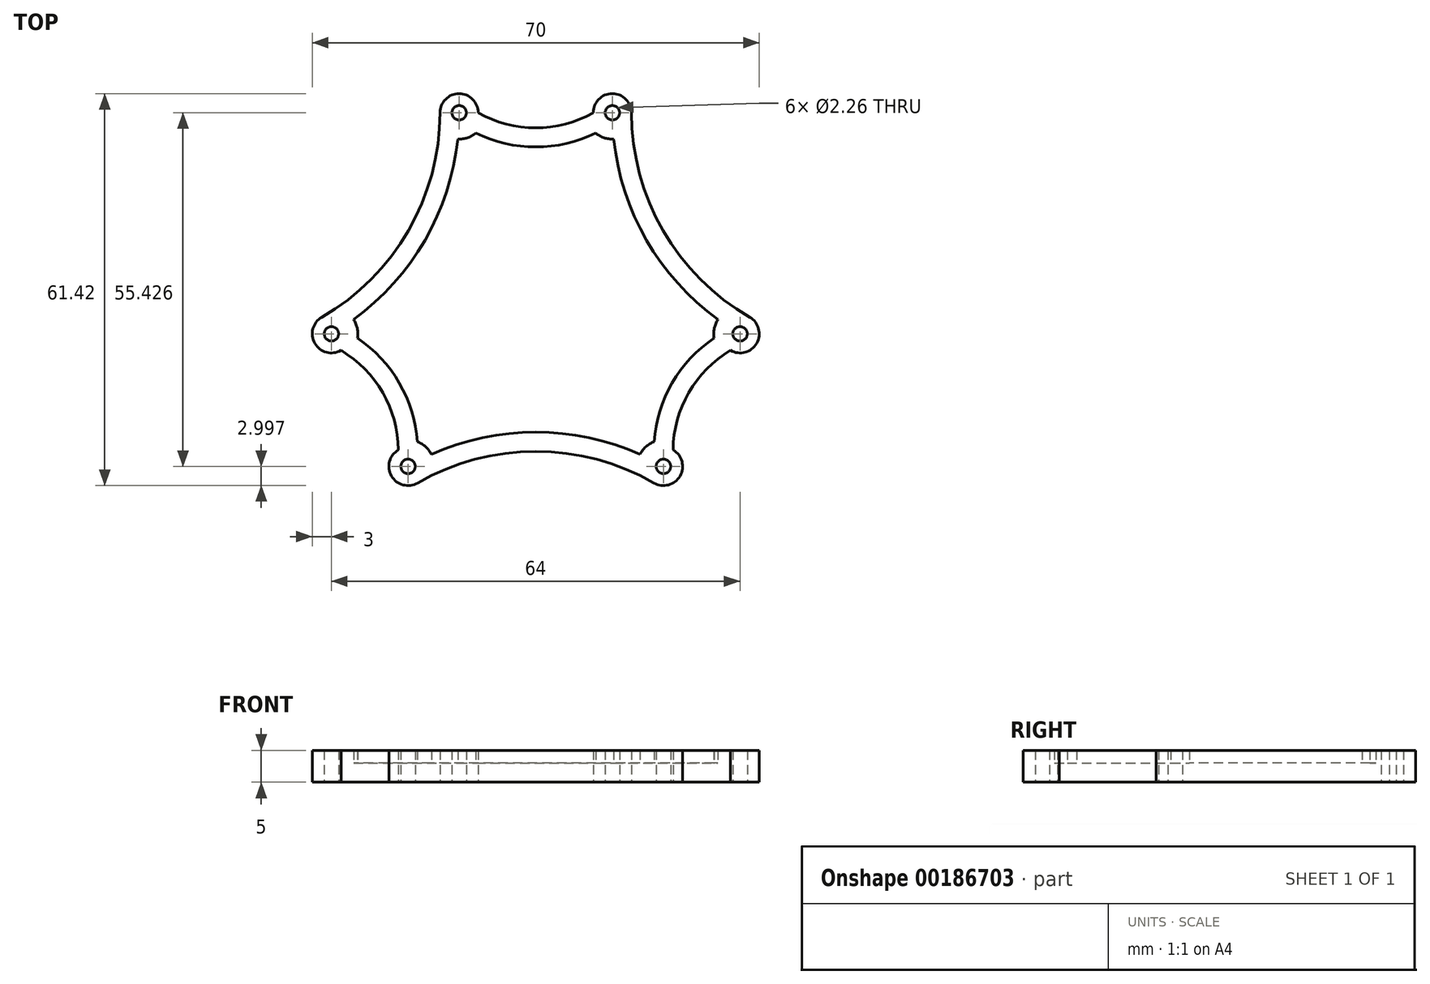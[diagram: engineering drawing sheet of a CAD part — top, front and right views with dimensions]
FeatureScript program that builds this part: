
annotation { "Feature Type Name" : "Feature", "Feature Type Description" : "" }
export const myFeature = defineFeature(function(context is Context, id is Id, definition is map)
    precondition{}
    {
        {
            var Q0;
            Q0=qCreatedBy(makeId("Top.planeOp"),FACE);
            var sketch = newSketch(context, id + "F0", { "sketchPlane" : qUnion([Q0])});
            skPoint(sketch, "E0.center", {"position": v(0, 0) * mm});
            skLineSegment(sketch, "E1", {"start": v(0, 0) * mm, "end": v(0, 30.02) * mm, "construction": true});
            skLineSegment(sketch, "E2", {"start": v(0, 30.02) * mm, "end": v(-12, 30.02) * mm, "construction": true});
            skLineSegment(sketch, "E3", {"start": v(0, 30.02) * mm, "end": v(12, 30.02) * mm, "construction": true});
            skLineSegment(sketch, "E4", {"start": v(0, 0) * mm, "end": v(26, -15.01) * mm, "construction": true});
            skLineSegment(sketch, "E5", {"start": v(32, -4.62) * mm, "end": v(26, -15.01) * mm, "construction": true});
            skLineSegment(sketch, "E6", {"start": v(20, -25.4) * mm, "end": v(26, -15.01) * mm, "construction": true});
            skLineSegment(sketch, "E7", {"start": v(0, 0) * mm, "end": v(-26, -15.01) * mm, "construction": true});
            skLineSegment(sketch, "E8", {"start": v(-20, -25.4) * mm, "end": v(-26, -15.01) * mm, "construction": true});
            skLineSegment(sketch, "E9", {"start": v(-32, -4.62) * mm, "end": v(-26, -15.01) * mm, "construction": true});
            skCircle(sketch, "E10", {"center": v(0, 0) * mm, "radius": 20 * mm, "construction": true});
            skSolve(sketch);
        }
        {
            var Q0;
            Q0=qCreatedBy(makeId("Top.planeOp"),FACE);
            var sketch = newSketch(context, id + "F1", { "sketchPlane" : qUnion([Q0])});
            skArc(sketch, "E11", {"start": v(-9, 30.02) * mm, "mid": v(-12, 33.02) * mm, "end": v(-15, 30.02) * mm});
            skArc(sketch, "E12.MirrorCS", {"start": v(9, 30.02) * mm, "mid": v(12, 33.02) * mm, "end": v(15, 30.02) * mm});
            skArc(sketch, "E13", {"start": v(-9, 30.02) * mm, "mid": v(0, 27.67) * mm, "end": v(9, 30.02) * mm});
            skArc(sketch, "E14.1.2", {"start": v(21.5, -22.8) * mm, "mid": v(22.6, -26.9) * mm, "end": v(18.5, -28) * mm});
            skArc(sketch, "E14.1.3", {"start": v(30.5, -7.22) * mm, "mid": v(23.96, -13.83) * mm, "end": v(21.5, -22.8) * mm});
            skArc(sketch, "E14.1.4", {"start": v(30.5, -7.22) * mm, "mid": v(34.6, -6.12) * mm, "end": v(33.5, -2.02) * mm});
            skArc(sketch, "E14.2.2", {"start": v(-30.5, -7.22) * mm, "mid": v(-34.6, -6.12) * mm, "end": v(-33.5, -2.02) * mm});
            skArc(sketch, "E14.2.3", {"start": v(-21.5, -22.8) * mm, "mid": v(-23.96, -13.83) * mm, "end": v(-30.5, -7.22) * mm});
            skArc(sketch, "E14.2.4", {"start": v(-21.5, -22.8) * mm, "mid": v(-22.6, -26.9) * mm, "end": v(-18.5, -28) * mm});
            skPoint(sketch, "E14.center", {"position": v(0, 0) * mm});
            skLineSegment(sketch, "E14.anchor1", {"start": v(0, 0) * mm, "end": v(-15, 13.23) * mm, "construction": true});
            skLineSegment(sketch, "E14.anchor2", {"start": v(0, 0) * mm, "end": v(-3.96, -19.6) * mm, "construction": true});
            skArc(sketch, "E15", {"start": v(15, 30.02) * mm, "mid": v(19.96, 11.52) * mm, "end": v(33.5, -2.02) * mm});
            skArc(sketch, "E16.1.0", {"start": v(-33.5, -2.02) * mm, "mid": v(-19.96, 11.52) * mm, "end": v(-15, 30.02) * mm});
            skArc(sketch, "E16.2.0", {"start": v(18.5, -28) * mm, "mid": v(0, -23.04) * mm, "end": v(-18.5, -28) * mm});
            skSolve(sketch);
        }
        {
            var Q0;
            Q0=makeQuery(id+"F1.imprint","IMPRINT",FACE,{"disambiguationData":[TD([[makeQuery(id+"F1.imprint","IMPRINT",EDGE,{"derivedFrom":sQuery(id+"F1.wireOp",EDGE,"E11")}),1.0]])]});
            extrude(context, id + "F2", {"entities" : qUnion([Q0]), "depth" : 5 * mm});
        }
        {
            var Q0;
            Q0=sQuery(id+"F0.wireOp",VERTEX,"E2.end");
            var Q1;
            Q1=sQuery(id+"F0.wireOp",VERTEX,"E3.end");
            var Q2;
            Q2=sQuery(id+"F0.wireOp",VERTEX,"E5.start");
            var Q3;
            Q3=sQuery(id+"F0.wireOp",VERTEX,"E6.start");
            var Q4;
            Q4=sQuery(id+"F0.wireOp",VERTEX,"E8.start");
            var Q5;
            Q5=sQuery(id+"F0.wireOp",VERTEX,"E9.start");
            var Q6;
            Q6=makeQuery(id+"F2.opExtrude","SWEPT_BODY",BODY,{"disambiguationData":[OSD([sQuery(id+"F1.wireOp",EDGE,"E11"),sQuery(id+"F1.wireOp",EDGE,"eSNNaFJx-W7Ud-ONSg-WrLk-HhzJiakDTCRT"),sQuery(id+"F1.wireOp",EDGE,"55ARqof1-Wp8X-i2ir-1X07-WUa1pFoOfkcR"),sQuery(id+"F1.wireOp",EDGE,"FQYiC6e6-v0yu-UJcv-DbZK-kRTUjw7TfWA4")])]});
            hole(context, id + "F3", {"style" : HoleStyle.SIMPLE, "endStyle" : HoleEndStyle.THROUGH, "oppositeDirection" : true, "standardTappedOrClearance" : lookupTablePath({ "standard" : "ANSI", "engagement" : "75%", "pitch" : "40 tpi", "size" : "#4", "type" : "Tapped" }), "standardBlindInLast" : lookupTablePath({ "standard" : "ANSI", "engagement" : "75%", "pitch" : "40 tpi", "size" : "#4", "type" : "Tapped" }), "holeDiameter" : 2.26 * mm, "locations" : qUnion([Q0, Q1, Q2, Q3, Q4, Q5]), "scope" : qUnion([Q6]), "isTappedThrough" : true, "majorDiameter" : 2.84 * mm, "showTappedDepth" : true});
        }
        {
            var Q0;
            Q0=makeQuery(id+"F2.opExtrude","CAP_FACE",FACE,{"disambiguationData":[OSD([sQuery(id+"F1.wireOp",EDGE,"E11"),sQuery(id+"F1.wireOp",EDGE,"E12.MirrorCS"),sQuery(id+"F1.wireOp",EDGE,"E13"),sQuery(id+"F1.wireOp",EDGE,"E14.1.2"),sQuery(id+"F1.wireOp",EDGE,"E14.1.3"),sQuery(id+"F1.wireOp",EDGE,"E14.1.4"),sQuery(id+"F1.wireOp",EDGE,"E14.2.2"),sQuery(id+"F1.wireOp",EDGE,"E14.2.3"),sQuery(id+"F1.wireOp",EDGE,"E14.2.4"),sQuery(id+"F1.wireOp",EDGE,"E15"),sQuery(id+"F1.wireOp",EDGE,"E16.1.0"),sQuery(id+"F1.wireOp",EDGE,"E16.2.0")])],"isStart":false});
            shell(context, id + "F4", {"entities" : qUnion([Q0]), "thickness" : 3 * mm});
        }
    });
